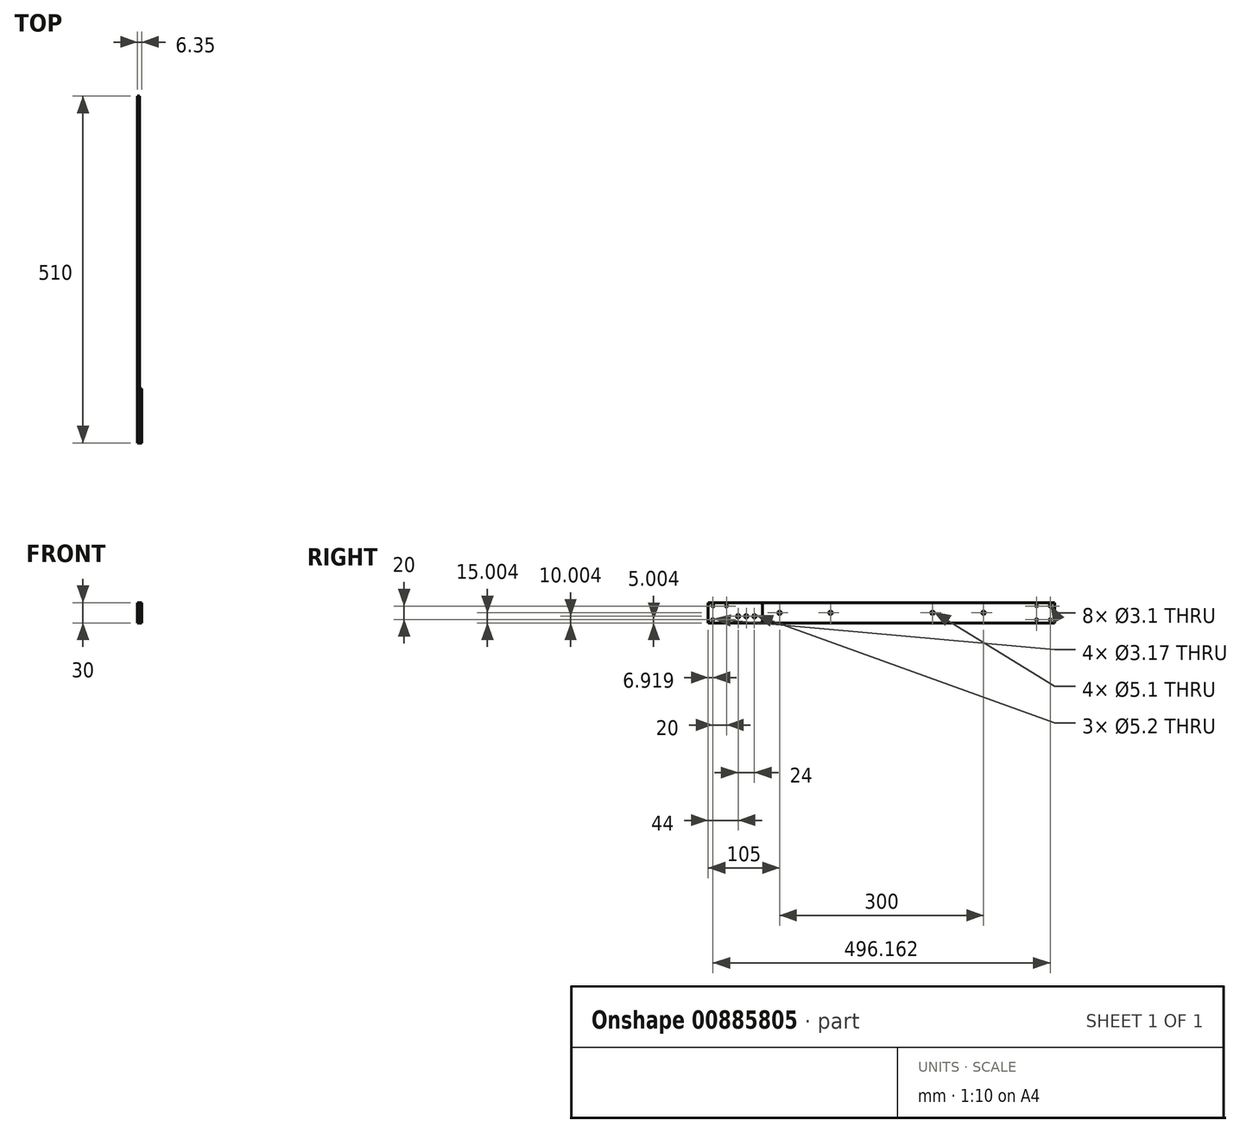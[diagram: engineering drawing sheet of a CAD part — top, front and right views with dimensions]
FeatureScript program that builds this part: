
annotation { "Feature Type Name" : "Feature", "Feature Type Description" : "" }
export const myFeature = defineFeature(function(context is Context, id is Id, definition is map)
    precondition{}
    {
        {
            var Q0;
            Q0=qCreatedBy(makeId("Front.planeOp"),FACE);
            var sketch = newSketch(context, id + "F0", { "sketchPlane" : qUnion([Q0])});
            skLineSegment(sketch, "E0.bottom", {"start": v(-35.69, 64.01) * mm, "end": v(-32.51, 64.01) * mm});
            skLineSegment(sketch, "E0.top", {"start": v(-35.69, 34.01) * mm, "end": v(-32.51, 34.01) * mm});
            skLineSegment(sketch, "E0.left", {"start": v(-35.69, 64.01) * mm, "end": v(-35.69, 34.01) * mm});
            skLineSegment(sketch, "E0.right", {"start": v(-32.51, 64.01) * mm, "end": v(-32.51, 34.01) * mm});
            skSolve(sketch);
        }
        {
            var Q0;
            Q0=qSketchRegion(id+"F0",true);
            extrude(context, id + "F1", {"entities" : qUnion([Q0]), "depth" : 255 * mm, "offsetDistance" : 25 * mm});
        }
        {
            var Q0;
            Q0=makeQuery(id+"F1.opExtrude","SWEPT_FACE",FACE,{"disambiguationData":[OSD([sQuery(id+"F0.wireOp",EDGE,"E0.right")])]});
            var sketch = newSketch(context, id + "F2", { "sketchPlane" : qUnion([Q0])});
            skCircle(sketch, "E1", {"center": v(-228.08, 59.01) * mm, "radius": 1.55 * mm});
            skCircle(sketch, "E2", {"center": v(-228.08, 39.01) * mm, "radius": 1.55 * mm});
            skCircle(sketch, "E3", {"center": v(-248.08, 59.01) * mm, "radius": 1.55 * mm});
            skCircle(sketch, "E4", {"center": v(-248.08, 39.01) * mm, "radius": 1.55 * mm});
            skCircle(sketch, "E5", {"center": v(-150, 49.01) * mm, "radius": 2.55 * mm});
            skCircle(sketch, "E6", {"center": v(-75, 49.01) * mm, "radius": 2.55 * mm});
            skSolve(sketch);
        }
        {
            var Q0;
            Q0=makeQuery(id+"F2.imprint","IMPRINT",FACE,{"disambiguationData":[TD([[makeQuery(id+"F2.imprint","IMPRINT",EDGE,{"derivedFrom":sQuery(id+"F2.wireOp",EDGE,"E3")}),1.0]])]});
            var Q1;
            Q1=makeQuery(id+"F2.imprint","IMPRINT",FACE,{"disambiguationData":[TD([[makeQuery(id+"F2.imprint","IMPRINT",EDGE,{"derivedFrom":sQuery(id+"F2.wireOp",EDGE,"E1")}),1.0]])]});
            var Q2;
            Q2=makeQuery(id+"F2.imprint","IMPRINT",FACE,{"disambiguationData":[TD([[makeQuery(id+"F2.imprint","IMPRINT",EDGE,{"derivedFrom":sQuery(id+"F2.wireOp",EDGE,"E2")}),1.0]])]});
            var Q3;
            Q3=makeQuery(id+"F2.imprint","IMPRINT",FACE,{"disambiguationData":[TD([[makeQuery(id+"F2.imprint","IMPRINT",EDGE,{"derivedFrom":sQuery(id+"F2.wireOp",EDGE,"E4")}),1.0]])]});
            var Q4;
            Q4=makeQuery(id+"F2.imprint","IMPRINT",FACE,{"disambiguationData":[TD([[makeQuery(id+"F2.imprint","IMPRINT",EDGE,{"derivedFrom":sQuery(id+"F2.wireOp",EDGE,"E5")}),1.0]])]});
            var Q5;
            Q5=makeQuery(id+"F2.imprint","IMPRINT",FACE,{"disambiguationData":[TD([[makeQuery(id+"F2.imprint","IMPRINT",EDGE,{"derivedFrom":sQuery(id+"F2.wireOp",EDGE,"E6")}),1.0]])]});
            extrude(context, id + "F3", {"entities" : qUnion([Q0, Q1, Q2, Q3, Q4, Q5]), "operationType" : NewBodyOperationType.REMOVE, "oppositeDirection" : true, "depth" : 25 * mm, "offsetDistance" : 25 * mm});
        }
        {
            var Q0;
            Q0=makeQuery(id+"F1.opExtrude","SWEPT_BODY",BODY,{"disambiguationData":[OSD([sQuery(id+"F0.wireOp",EDGE,"E0.bottom"),sQuery(id+"F0.wireOp",EDGE,"E0.top"),sQuery(id+"F0.wireOp",EDGE,"E0.left"),sQuery(id+"F0.wireOp",EDGE,"E0.right")])]});
            var Q1;
            Q1=makeQuery(id+"F1.opExtrude","CAP_FACE",FACE,{"disambiguationData":[OSD([sQuery(id+"F0.wireOp",EDGE,"E0.bottom"),sQuery(id+"F0.wireOp",EDGE,"E0.top"),sQuery(id+"F0.wireOp",EDGE,"E0.left"),sQuery(id+"F0.wireOp",EDGE,"E0.right")])],"isStart":true});
            mirror(context, id + "F4", {"operationType" : NewBodyOperationType.ADD, "entities" : qUnion([Q0]), "mirrorPlane" : qUnion([Q1])});
        }
        {
            var Q0;
            {var subQ0=makeQuery(id+"F1.opExtrude","SWEPT_FACE",FACE,{"disambiguationData":[OSD([sQuery(id+"F0.wireOp",EDGE,"E0.right")])]});Q0=makeQuery(id+"F4.boolean.opBoolean","MERGE",FACE,{"derivedFrom":[subQ0,makeQuery(id+"F4.opPattern","COPY",FACE,{"derivedFrom":subQ0,"instanceName":"1"})]});}
            var sketch = newSketch(context, id + "F5", { "sketchPlane" : qUnion([Q0])});
            skLineSegment(sketch, "E7.bottom", {"start": v(-250, 64.01) * mm, "end": v(-180, 64.01) * mm});
            skLineSegment(sketch, "E7.top", {"start": v(-250, 34.01) * mm, "end": v(-180, 34.01) * mm});
            skLineSegment(sketch, "E7.left", {"start": v(-255, 59.01) * mm, "end": v(-255, 39.01) * mm});
            skLineSegment(sketch, "E7.right", {"start": v(-175, 59.01) * mm, "end": v(-175, 39.01) * mm});
            skCircle(sketch, "E8", {"center": v(-248.08, 59.01) * mm, "radius": 1.59 * mm});
            skCircle(sketch, "E9", {"center": v(-228.08, 59.01) * mm, "radius": 1.59 * mm});
            skCircle(sketch, "E10", {"center": v(-228.08, 39.01) * mm, "radius": 1.59 * mm});
            skCircle(sketch, "E11", {"center": v(-248.08, 39.01) * mm, "radius": 1.59 * mm});
            skCircle(sketch, "E12", {"center": v(-211, 44.01) * mm, "radius": 2.6 * mm});
            skCircle(sketch, "E13", {"center": v(-199, 44.01) * mm, "radius": 2.6 * mm});
            skCircle(sketch, "E14", {"center": v(-187, 44.01) * mm, "radius": 2.6 * mm});
            skPoint(sketch, "E15.visualSharp", {"position": v(-255, 64.01) * mm});
            skArc(sketch, "E15.filletArc", {"start": v(-250, 64.01) * mm, "mid": v(-253.54, 62.55) * mm, "end": v(-255, 59.01) * mm});
            skPoint(sketch, "E16.visualSharp", {"position": v(-255, 34.01) * mm});
            skArc(sketch, "E16.filletArc", {"start": v(-255, 39.01) * mm, "mid": v(-253.54, 35.48) * mm, "end": v(-250, 34.01) * mm});
            skPoint(sketch, "E17.visualSharp", {"position": v(-175, 34.01) * mm});
            skArc(sketch, "E17.filletArc", {"start": v(-180, 34.01) * mm, "mid": v(-176.46, 35.48) * mm, "end": v(-175, 39.01) * mm});
            skPoint(sketch, "E18.visualSharp", {"position": v(-175, 64.01) * mm});
            skArc(sketch, "E18.filletArc", {"start": v(-175, 59.01) * mm, "mid": v(-176.46, 62.55) * mm, "end": v(-180, 64.01) * mm});
            skSolve(sketch);
        }
        {
            var Q0;
            Q0 = qSketchRegion(id + "F5", true);
            extrude(context, id + "F6", {"entities" : qUnion([Q0]), "depth" : 3.17 * mm, "offsetDistance" : 25 * mm});
        }
    });
